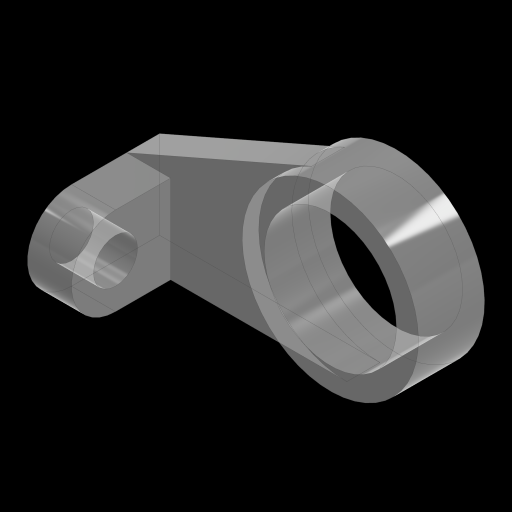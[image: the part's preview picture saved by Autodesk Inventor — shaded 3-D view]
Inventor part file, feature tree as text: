
AUTODESK INVENTOR PART (.ipt)
format: ipt  version: 2024 (Build 280153000, 153)  size: 169,472 bytes
history: native  units: in
note: dims shown in document units (in); Inventor stores cm internally (conversion verified against a paired STEP export)
features: sketch x6, extrude x4, hole x2
ambient origin geometry x8: Origin, YZ Plane, XZ Plane, XY Plane, X Axis, Y Axis, Z Axis, Center Point
bodies: Solid1 (feature_tree)
feature tree (12):
  extrude  "MAIN BODY"  Depth=5.0in
  extrude  "MAIN BODY LIP"  Depth=0.75in TaperAngle=0.0deg
  extrude  "SIDE EXT"  Depth=1.5in TaperAngle=0.0deg
  extrude  "SIDE EXT CURVE"  Depth=2.0in
  hole  "SIDE EXT HOLE"  [1 undecoded]
  hole  "MAIN BODY HOLE"  [1 undecoded]
  sketch  "Sketch1"  dims[d0=5.0in d1=4.0in]
  sketch  "Sketch2"  dims[d2=2.0in d3=0.75in d4=0.0in]
  sketch  "Sketch3"  dims[d5=4.0in d6=1.5in d7=0.0in]
  sketch  "Sketch4"  dims[d8=1.0in d9=2.0in]
  sketch  "Sketch5"  dims[d10=1.25in d11=0.0in d12=1.0in d13=0.0in]
  sketch  "Sketch6"  dims[d14=1.0in d15=0.75in d16=0.375in d17=0.25in d18=0.5635in d19=1.0in d20=0.8108in d21=3.0in d22=0.75in d23=0.375in d24=0.25in d25=0.5635in d26=1.0in d27=0.8108in]
note: 2 required parameter values undecoded (feature->parameter linkage not recoverable at this tier; creation-order binding heuristic only, values carry confidence <= 0.55)
